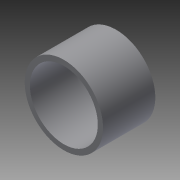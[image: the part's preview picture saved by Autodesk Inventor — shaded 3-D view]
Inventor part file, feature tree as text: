
AUTODESK INVENTOR PART (.ipt)
format: ipt  version: 2015 (Build 190159000, 159)  size: 93,696 bytes
history: native  units: mm
features: extrude x2, sketch x2
ambient origin geometry x8: Origin, YZ Plane, XZ Plane, XY Plane, X Axis, Y Axis, Z Axis, Center Point
bodies: Solid1 (feature_tree)
feature tree (4):
  extrude  "Extrusion1"  Depth=26.0mm
  extrude  "Extrusion2"  Depth=3.0mm
  sketch  "Sketch1"  dims[d0=30.0mm d1=26.0mm]
  sketch  "Sketch2"  dims[d2=20.0mm d3=0.0mm d4=28.0mm d5=26.0mm d6=3.0mm d7=0.0mm]
